# Revit family: Furniture-Lighted_Mirror_Cabinet-KOHLER-MAXSTOW-K-23958T
name_source: partatom
category: Lighting Fixtures
units: mm (PartAtom-declared; Revit-internal decimal feet)

## family parameters
Cut with Voids When Loaded = No
Host = Face
Light Source = Yes
OmniClass Number = 23.25.53.11.13.11
OmniClass Title = Medicine Cabinet
Part Type = Normal
Room Calculation Point = No
Round Connector Dimension = Use Diameter
Shared = No

## types (1)
- NA-Mild Silver
    ADA Compliant = Yes
    Apparent Load = 40 VA
    Assembly Code = E2010
    Color Filter = 16777215
    Date Modified = 01/23/2023
    Default Elevation = 60"
    Description = Medicine Cabinet
    Dimming Lamp Color Temperature Shift = Incandescent Lamp Curve
    Electrical Connector = Yes
    Electrical Note = One Dedicated Circuit Required
    Emit from Line Length = 40"
    Finish = KOHLER-Metal-NA-Mild_Silver
    Hardware Included = No
    Height = 48 1/2"
    Lamp = LED
    Length = 6"
    Light Source Symbol Size = 6"
    Manufacturer = Kohler Co.
    Master Format 2014 = 41 53 13
    Master Format 2014 Name = Storage Cabinets
    Material = Aluminium
    Model = K-23958T-NA
    Product Name = MAXSTOW
    Type = 1
    URL = http://www.kohler.com.cn
    Voltage = 220 V
    WaterSense Certified = No
    Wattage Comments = 40W
    Width = 50 3/8"

## geometry (parser evidence)
native form markers: Sweep x10
no freeform markers — native parametric forms only
